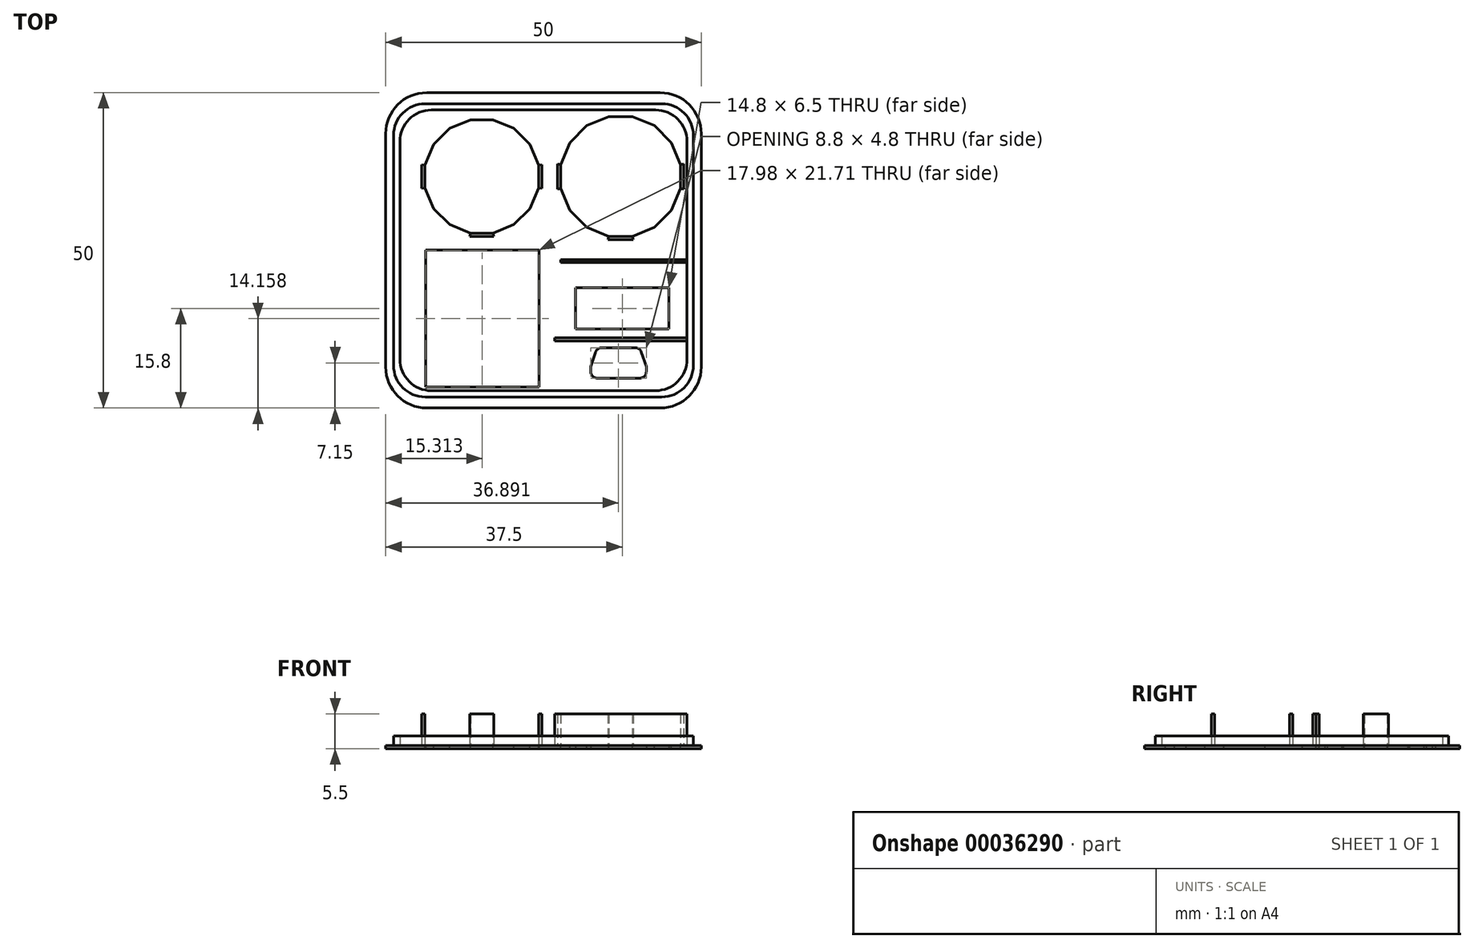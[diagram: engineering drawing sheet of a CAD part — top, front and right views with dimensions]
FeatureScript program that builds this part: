
annotation { "Feature Type Name" : "Feature", "Feature Type Description" : "" }
export const myFeature = defineFeature(function(context is Context, id is Id, definition is map)
    precondition{}
    {
        {
            var Q0;
            Q0=qCreatedBy(makeId("Top.planeOp"),FACE);
            var sketch = newSketch(context, id + "F0", { "sketchPlane" : qUnion([Q0])});
            skLineSegment(sketch, "E0.bottom", {"start": v(6.5, 0) * mm, "end": v(43.5, 0) * mm});
            skLineSegment(sketch, "E0.top", {"start": v(6.5, -50) * mm, "end": v(43.5, -50) * mm});
            skLineSegment(sketch, "E0.left", {"start": v(0, -6.5) * mm, "end": v(0, -43.5) * mm});
            skLineSegment(sketch, "E0.right", {"start": v(50, -6.5) * mm, "end": v(50, -43.5) * mm});
            skPoint(sketch, "E1.visualSharp", {"position": v(0, 0) * mm});
            skArc(sketch, "E1.filletArc", {"start": v(6.5, 0) * mm, "mid": v(1.9, -1.9) * mm, "end": v(0, -6.5) * mm});
            skPoint(sketch, "E2.visualSharp", {"position": v(50, 0) * mm});
            skArc(sketch, "E2.filletArc", {"start": v(50, -6.5) * mm, "mid": v(48.1, -1.9) * mm, "end": v(43.5, 0) * mm});
            skPoint(sketch, "E3.visualSharp", {"position": v(50, -50) * mm});
            skArc(sketch, "E3.filletArc", {"start": v(43.5, -50) * mm, "mid": v(48.1, -48.1) * mm, "end": v(50, -43.5) * mm});
            skPoint(sketch, "E4.visualSharp", {"position": v(0, -50) * mm});
            skArc(sketch, "E4.filletArc", {"start": v(0, -43.5) * mm, "mid": v(1.9, -48.1) * mm, "end": v(6.5, -50) * mm});
            skSolve(sketch);
        }
        {
            var Q0;
            Q0=qSketchRegion(id+"FKO5VP6ajgZ1Vob_0",true);
            var Q1;
            Q1=makeQuery(id+"F0.imprint","IMPRINT",FACE,{"disambiguationData":[TD([[makeQuery(id+"F0.imprint","IMPRINT",EDGE,{"derivedFrom":sQuery(id+"F0.wireOp",EDGE,"E0.bottom")}),-1.0]])]});
            extrude(context, id + "F1", {"entities" : qUnion([Q0, Q1]), "depth" : 0.5 * mm});
        }
        {
            var Q0;
            Q0=makeQuery(id+"F1.opExtrude","CAP_FACE",FACE,{"disambiguationData":[OSD([sQuery(id+"F0.wireOp",EDGE,"E0.bottom"),sQuery(id+"F0.wireOp",EDGE,"E0.top"),sQuery(id+"F0.wireOp",EDGE,"E0.left"),sQuery(id+"F0.wireOp",EDGE,"E0.right")])],"isStart":false});
            var sketch = newSketch(context, id + "F2", { "sketchPlane" : qUnion([Q0])});
            skLineSegment(sketch, "E5.bottom", {"start": v(6.25, -1.75) * mm, "end": v(43.75, -1.75) * mm});
            skLineSegment(sketch, "E5.top", {"start": v(6.25, -48.25) * mm, "end": v(43.75, -48.25) * mm});
            skLineSegment(sketch, "E5.left", {"start": v(1.25, -6.75) * mm, "end": v(1.25, -43.25) * mm});
            skLineSegment(sketch, "E5.right", {"start": v(48.75, -6.75) * mm, "end": v(48.75, -43.25) * mm});
            skLineSegment(sketch, "E6", {"start": v(25, 0) * mm, "end": v(25, -1.75) * mm, "construction": true});
            skLineSegment(sketch, "E7", {"start": v(25, -48.25) * mm, "end": v(25, -50) * mm, "construction": true});
            skLineSegment(sketch, "E8.0", {"start": v(7.25, -2.75) * mm, "end": v(42.75, -2.75) * mm});
            skLineSegment(sketch, "E8.1", {"start": v(2.25, -7.75) * mm, "end": v(2.25, -42.25) * mm});
            skLineSegment(sketch, "E8.2", {"start": v(7.25, -47.25) * mm, "end": v(42.75, -47.25) * mm});
            skLineSegment(sketch, "E8.3", {"start": v(47.75, -7.75) * mm, "end": v(47.75, -42.25) * mm});
            skPoint(sketch, "E9.visualSharp", {"position": v(2.25, -2.75) * mm});
            skArc(sketch, "E9.filletArc", {"start": v(7.25, -2.75) * mm, "mid": v(3.71, -4.21) * mm, "end": v(2.25, -7.75) * mm});
            skPoint(sketch, "E10.visualSharp", {"position": v(1.25, -1.75) * mm});
            skArc(sketch, "E10.filletArc", {"start": v(6.25, -1.75) * mm, "mid": v(2.71, -3.21) * mm, "end": v(1.25, -6.75) * mm});
            skPoint(sketch, "E11.visualSharp", {"position": v(48.75, -1.75) * mm});
            skArc(sketch, "E11.filletArc", {"start": v(48.75, -6.75) * mm, "mid": v(47.29, -3.21) * mm, "end": v(43.75, -1.75) * mm});
            skPoint(sketch, "E12.visualSharp", {"position": v(47.75, -2.75) * mm});
            skArc(sketch, "E12.filletArc", {"start": v(47.75, -7.75) * mm, "mid": v(46.29, -4.21) * mm, "end": v(42.75, -2.75) * mm});
            skPoint(sketch, "E13.visualSharp", {"position": v(47.75, -47.25) * mm});
            skArc(sketch, "E13.filletArc", {"start": v(42.75, -47.25) * mm, "mid": v(46.29, -45.79) * mm, "end": v(47.75, -42.25) * mm});
            skPoint(sketch, "E14.visualSharp", {"position": v(48.75, -48.25) * mm});
            skArc(sketch, "E14.filletArc", {"start": v(43.75, -48.25) * mm, "mid": v(47.29, -46.79) * mm, "end": v(48.75, -43.25) * mm});
            skPoint(sketch, "E15.visualSharp", {"position": v(2.25, -47.25) * mm});
            skArc(sketch, "E15.filletArc", {"start": v(2.25, -42.25) * mm, "mid": v(3.71, -45.79) * mm, "end": v(7.25, -47.25) * mm});
            skPoint(sketch, "E16.visualSharp", {"position": v(1.25, -48.25) * mm});
            skArc(sketch, "E16.filletArc", {"start": v(1.25, -43.25) * mm, "mid": v(2.71, -46.79) * mm, "end": v(6.25, -48.25) * mm});
            skSolve(sketch);
        }
        {
            var Q0;
            Q0=makeQuery(id+"F2.imprint","IMPRINT",FACE,{"disambiguationData":[TD([[makeQuery(id+"F2.imprint","IMPRINT",EDGE,{"derivedFrom":sQuery(id+"F2.wireOp",EDGE,"E5.bottom")}),1.0]])]});
            var sketch = newSketch(context, id + "F3", { "sketchPlane" : qUnion([Q0])});
            skSolve(sketch);
        }
        {
            var Q0;
            Q0=qSketchRegion(id+"F3",true);
            var Q1;
            Q1=makeQuery(id+"F2.imprint","IMPRINT",FACE,{"disambiguationData":[TD([[makeQuery(id+"F2.imprint","IMPRINT",EDGE,{"derivedFrom":sQuery(id+"F2.wireOp",EDGE,"E5.bottom")}),-1.0]])]});
            extrude(context, id + "F4", {"entities" : qUnion([Q0, Q1]), "operationType" : NewBodyOperationType.ADD, "depth" : 1.5 * mm});
        }
        {
            var Q0;
            Q0=makeQuery(id+"F1.opExtrude","CAP_FACE",FACE,{"disambiguationData":[OSD([sQuery(id+"F0.wireOp",EDGE,"E0.bottom"),sQuery(id+"F0.wireOp",EDGE,"E0.top"),sQuery(id+"F0.wireOp",EDGE,"E0.left"),sQuery(id+"F0.wireOp",EDGE,"E0.right"),sQuery(id+"F0.wireOp",EDGE,"E1.filletArc"),sQuery(id+"F0.wireOp",EDGE,"E2.filletArc"),sQuery(id+"F0.wireOp",EDGE,"E3.filletArc"),sQuery(id+"F0.wireOp",EDGE,"E4.filletArc")])],"isStart":true});
            var sketch = newSketch(context, id + "F5", { "sketchPlane" : qUnion([Q0])});
            skLineSegment(sketch, "E17.top", {"start": v(33.5, 45.25) * mm, "end": v(40.3, 45.25) * mm});
            skLineSegment(sketch, "E17.left", {"start": v(32.5, 43.45) * mm, "end": v(32.5, 44.25) * mm});
            skLineSegment(sketch, "E17.right", {"start": v(41.3, 43.45) * mm, "end": v(41.3, 44.25) * mm});
            skLineSegment(sketch, "E18.bottom", {"start": v(6.32, 24.99) * mm, "end": v(24.3, 24.99) * mm});
            skLineSegment(sketch, "E18.top", {"start": v(6.32, 46.7) * mm, "end": v(24.3, 46.7) * mm});
            skLineSegment(sketch, "E18.left", {"start": v(6.32, 24.99) * mm, "end": v(6.32, 46.7) * mm});
            skLineSegment(sketch, "E18.right", {"start": v(24.3, 24.99) * mm, "end": v(24.3, 46.7) * mm});
            skPoint(sketch, "E19.visualSharp", {"position": v(32.5, 45.25) * mm});
            skArc(sketch, "E19.filletArc", {"start": v(33.5, 45.25) * mm, "mid": v(32.78, 44.96) * mm, "end": v(32.5, 44.25) * mm});
            skPoint(sketch, "E20.visualSharp", {"position": v(41.3, 45.25) * mm});
            skArc(sketch, "E20.filletArc", {"start": v(41.3, 44.25) * mm, "mid": v(41, 44.96) * mm, "end": v(40.3, 45.25) * mm});
            skLineSegment(sketch, "E21", {"start": v(34.21, 40.45) * mm, "end": v(39.57, 40.45) * mm});
            skLineSegment(sketch, "E22", {"start": v(32.5, 43.45) * mm, "end": v(33.26, 41.13) * mm});
            skLineSegment(sketch, "E23", {"start": v(40.52, 41.13) * mm, "end": v(41.3, 43.45) * mm});
            skPoint(sketch, "E24.visualSharp", {"position": v(33.5, 40.45) * mm});
            skArc(sketch, "E24.filletArc", {"start": v(33.26, 41.13) * mm, "mid": v(33.63, 40.64) * mm, "end": v(34.21, 40.45) * mm});
            skPoint(sketch, "E25.visualSharp", {"position": v(40.3, 40.45) * mm});
            skArc(sketch, "E25.filletArc", {"start": v(39.57, 40.45) * mm, "mid": v(40.16, 40.64) * mm, "end": v(40.52, 41.13) * mm});
            skLineSegment(sketch, "E26.bottom", {"start": v(30.1, 37.45) * mm, "end": v(44.9, 37.45) * mm});
            skLineSegment(sketch, "E26.top", {"start": v(30.1, 30.95) * mm, "end": v(44.9, 30.95) * mm});
            skLineSegment(sketch, "E26.left", {"start": v(30.1, 37.45) * mm, "end": v(30.1, 30.95) * mm});
            skLineSegment(sketch, "E26.right", {"start": v(44.9, 37.45) * mm, "end": v(44.9, 30.95) * mm});
            skLineSegment(sketch, "E27", {"start": v(37, 40.45) * mm, "end": v(37, 39.95) * mm, "construction": true});
            skLineSegment(sketch, "E28", {"start": v(37.5, 30.95) * mm, "end": v(37.5, 26.61) * mm, "construction": true});
            skSolve(sketch);
        }
        {
            var Q0;
            Q0=makeQuery(id+"F5.imprint","IMPRINT",FACE,{"disambiguationData":[TD([[makeQuery(id+"F5.imprint","IMPRINT",EDGE,{"derivedFrom":sQuery(id+"F5.wireOp",EDGE,"E18.bottom")}),1.0]])]});
            var Q1;
            Q1=makeQuery(id+"F5.imprint","IMPRINT",FACE,{"disambiguationData":[TD([[makeQuery(id+"F5.imprint","IMPRINT",EDGE,{"derivedFrom":sQuery(id+"F5.wireOp",EDGE,"E17.top")}),-1.0]])]});
            var Q2;
            Q2=makeQuery(id+"F5.imprint","IMPRINT",FACE,{"disambiguationData":[TD([[makeQuery(id+"F5.imprint","IMPRINT",EDGE,{"derivedFrom":sQuery(id+"F5.wireOp",EDGE,"E26.bottom")}),-1.0]])]});
            extrude(context, id + "F6", {"entities" : qUnion([Q0, Q1, Q2]), "operationType" : NewBodyOperationType.REMOVE, "endBound" : BoundingType.UP_TO_NEXT, "oppositeDirection" : true, "depth" : 25 * mm});
        }
        {
            var Q0;
            Q0=makeQuery(id+"F3.imprint","IMPRINT",FACE,{"disambiguationData":[TD([[makeQuery(id+"F3.imprint","IMPRINT",EDGE,{"derivedFrom":makeQuery(id+"F2.imprint","IMPRINT",EDGE,{"derivedFrom":sQuery(id+"F2.wireOp",EDGE,"E5.bottom")})}),-1.0]])]});
            var sketch = newSketch(context, id + "F7", { "sketchPlane" : qUnion([Q0])});
            skLineSegment(sketch, "E29.bottom", {"start": v(47.75, -39.35) * mm, "end": v(26.75, -39.35) * mm});
            skLineSegment(sketch, "E29.top", {"start": v(47.75, -38.85) * mm, "end": v(26.75, -38.85) * mm});
            skLineSegment(sketch, "E29.left", {"start": v(47.75, -39.35) * mm, "end": v(47.75, -38.85) * mm});
            skLineSegment(sketch, "E29.right", {"start": v(26.75, -39.35) * mm, "end": v(26.75, -38.85) * mm});
            skLineSegment(sketch, "E30.bottom", {"start": v(47.75, -26.95) * mm, "end": v(27.75, -26.95) * mm});
            skLineSegment(sketch, "E30.top", {"start": v(47.75, -26.45) * mm, "end": v(27.75, -26.45) * mm});
            skLineSegment(sketch, "E30.left", {"start": v(47.75, -26.95) * mm, "end": v(47.75, -26.45) * mm});
            skLineSegment(sketch, "E30.right", {"start": v(27.75, -26.95) * mm, "end": v(27.75, -26.45) * mm});
            skLineSegment(sketch, "E31", {"start": v(37.25, -39.35) * mm, "end": v(37.25, -39.85) * mm, "construction": true});
            skLineSegment(sketch, "E32", {"start": v(37.75, -26.95) * mm, "end": v(37.75, -27.9) * mm});
            skSolve(sketch);
        }
        {
            var Q0;
            Q0=qSketchRegion(id+"F7",true);
            extrude(context, id + "F8", {"entities" : qUnion([Q0]), "operationType" : NewBodyOperationType.ADD, "depth" : 5 * mm});
        }
        {
            var Q0;
            Q0=makeQuery(id+"F3.imprint","IMPRINT",FACE,{"disambiguationData":[TD([[makeQuery(id+"F3.imprint","IMPRINT",EDGE,{"derivedFrom":makeQuery(id+"F2.imprint","IMPRINT",EDGE,{"derivedFrom":sQuery(id+"F2.wireOp",EDGE,"E5.bottom")})}),-1.0]])]});
            var sketch = newSketch(context, id + "F9", { "sketchPlane" : qUnion([Q0])});
            skLineSegment(sketch, "E33.4", {"start": v(29.18, -18.67) * mm, "end": v(27.73, -15.18) * mm});
            skLineSegment(sketch, "E34", {"start": v(42.62, -21.34) * mm, "end": v(42.9, -21.77) * mm});
            skLineSegment(sketch, "E35.11", {"start": v(24.22, -15.08) * mm, "end": v(22.84, -18.39) * mm});
            skLineSegment(sketch, "E36.7", {"start": v(27.23, -15.28) * mm, "end": v(27.23, -11.3) * mm});
            skLineSegment(sketch, "E37.12", {"start": v(17.1, -3.8) * mm, "end": v(20.6, -5.24) * mm});
            skLineSegment(sketch, "E33.15", {"start": v(39.12, -3.8) * mm, "end": v(42.62, -5.24) * mm});
            skLineSegment(sketch, "E33.14", {"start": v(42.62, -5.24) * mm, "end": v(45.29, -7.9) * mm});
            skLineSegment(sketch, "E37.2", {"start": v(20.6, -21.34) * mm, "end": v(17.1, -22.8) * mm});
            skLineSegment(sketch, "E35.8", {"start": v(17, -22.3) * mm, "end": v(13.42, -22.3) * mm});
            skLineSegment(sketch, "E36.6", {"start": v(28.76, -18.95) * mm, "end": v(27.23, -15.28) * mm});
            skLineSegment(sketch, "E38", {"start": v(17, -22.3) * mm, "end": v(17.1, -22.8) * mm});
            skLineSegment(sketch, "E36.1", {"start": v(45.71, -18.95) * mm, "end": v(42.9, -21.77) * mm});
            skLineSegment(sketch, "E39", {"start": v(35.34, -22.8) * mm, "end": v(35.24, -23.3) * mm});
            skLineSegment(sketch, "E36.0", {"start": v(47.23, -15.28) * mm, "end": v(45.71, -18.95) * mm});
            skLineSegment(sketch, "E35.1", {"start": v(7.59, -8.2) * mm, "end": v(10.12, -5.66) * mm});
            skLineSegment(sketch, "E35.15", {"start": v(17, -4.3) * mm, "end": v(20.31, -5.66) * mm});
            skLineSegment(sketch, "E35.12", {"start": v(24.22, -11.5) * mm, "end": v(24.22, -15.08) * mm});
            skLineSegment(sketch, "E33.3", {"start": v(27.73, -15.18) * mm, "end": v(27.73, -11.4) * mm});
            skLineSegment(sketch, "E33.1", {"start": v(29.18, -7.9) * mm, "end": v(31.85, -5.24) * mm});
            skLineSegment(sketch, "E40", {"start": v(23.27, -18.67) * mm, "end": v(22.84, -18.39) * mm});
            skLineSegment(sketch, "E36.14", {"start": v(45.71, -7.63) * mm, "end": v(47.23, -11.3) * mm});
            skLineSegment(sketch, "E37.13", {"start": v(20.6, -5.24) * mm, "end": v(23.27, -7.9) * mm});
            skCircle(sketch, "E36.cCircle", {"center": v(37.23, -13.3) * mm, "radius": 10 * mm, "construction": true});
            skLineSegment(sketch, "E33.7", {"start": v(35.34, -22.8) * mm, "end": v(31.85, -21.34) * mm});
            skLineSegment(sketch, "E36.3", {"start": v(39.22, -23.3) * mm, "end": v(35.24, -23.3) * mm});
            skLineSegment(sketch, "E36.9", {"start": v(28.76, -7.63) * mm, "end": v(31.57, -4.81) * mm});
            skLineSegment(sketch, "E35.3", {"start": v(6.22, -15.08) * mm, "end": v(6.22, -11.5) * mm});
            skLineSegment(sketch, "E35.0", {"start": v(10.12, -5.66) * mm, "end": v(13.42, -4.3) * mm});
            skLineSegment(sketch, "E36.5", {"start": v(31.57, -21.77) * mm, "end": v(28.76, -18.95) * mm});
            skLineSegment(sketch, "E35.14", {"start": v(20.31, -5.66) * mm, "end": v(22.84, -8.2) * mm});
            skLineSegment(sketch, "E36.12", {"start": v(39.22, -3.3) * mm, "end": v(42.9, -4.81) * mm});
            skLineSegment(sketch, "E33.8", {"start": v(39.12, -22.8) * mm, "end": v(35.34, -22.8) * mm});
            skLineSegment(sketch, "E37.10", {"start": v(9.83, -5.24) * mm, "end": v(13.33, -3.8) * mm});
            skLineSegment(sketch, "E35.13", {"start": v(22.84, -8.2) * mm, "end": v(24.22, -11.5) * mm});
            skLineSegment(sketch, "E37.15", {"start": v(24.72, -11.4) * mm, "end": v(24.72, -15.18) * mm});
            skLineSegment(sketch, "E37.1", {"start": v(23.27, -18.67) * mm, "end": v(20.6, -21.34) * mm});
            skLineSegment(sketch, "E35.4", {"start": v(7.59, -18.39) * mm, "end": v(6.22, -15.08) * mm});
            skLineSegment(sketch, "E37.9", {"start": v(7.16, -7.9) * mm, "end": v(9.83, -5.24) * mm});
            skLineSegment(sketch, "E37.8", {"start": v(5.72, -11.4) * mm, "end": v(7.16, -7.9) * mm});
            skLineSegment(sketch, "E36.2", {"start": v(42.9, -21.77) * mm, "end": v(39.22, -23.3) * mm});
            skLineSegment(sketch, "E37.3", {"start": v(17.1, -22.8) * mm, "end": v(13.33, -22.8) * mm});
            skLineSegment(sketch, "E37.7", {"start": v(5.72, -15.18) * mm, "end": v(5.72, -11.4) * mm});
            skLineSegment(sketch, "E35.10", {"start": v(22.84, -18.39) * mm, "end": v(20.31, -20.92) * mm});
            skLineSegment(sketch, "E36.10", {"start": v(31.57, -4.81) * mm, "end": v(35.24, -3.3) * mm});
            skLineSegment(sketch, "E37.5", {"start": v(9.83, -21.34) * mm, "end": v(7.16, -18.67) * mm});
            skLineSegment(sketch, "E35.9", {"start": v(20.31, -20.92) * mm, "end": v(17, -22.3) * mm});
            skLineSegment(sketch, "E33.10", {"start": v(45.29, -18.67) * mm, "end": v(42.62, -21.34) * mm});
            skLineSegment(sketch, "E37.6", {"start": v(7.16, -18.67) * mm, "end": v(5.72, -15.18) * mm});
            skLineSegment(sketch, "E33.13", {"start": v(45.29, -7.9) * mm, "end": v(46.73, -11.4) * mm});
            skLineSegment(sketch, "E36.4", {"start": v(35.24, -23.3) * mm, "end": v(31.57, -21.77) * mm});
            skLineSegment(sketch, "E33.0", {"start": v(31.85, -5.24) * mm, "end": v(35.34, -3.8) * mm});
            skLineSegment(sketch, "E33.12", {"start": v(46.73, -11.4) * mm, "end": v(46.73, -15.18) * mm});
            skLineSegment(sketch, "E36.8", {"start": v(27.23, -11.3) * mm, "end": v(28.76, -7.63) * mm});
            skLineSegment(sketch, "E41", {"start": v(13.33, -22.8) * mm, "end": v(13.42, -22.3) * mm});
            skLineSegment(sketch, "E33.6", {"start": v(31.85, -21.34) * mm, "end": v(29.18, -18.67) * mm});
            skLineSegment(sketch, "E33.11", {"start": v(46.73, -15.18) * mm, "end": v(45.29, -18.67) * mm});
            skLineSegment(sketch, "E37.4", {"start": v(13.33, -22.8) * mm, "end": v(9.83, -21.34) * mm});
            skLineSegment(sketch, "E36.13", {"start": v(42.9, -4.81) * mm, "end": v(45.71, -7.63) * mm});
            skPoint(sketch, "E37.0.midPoint", {"position": v(24, -16.93) * mm});
            skLineSegment(sketch, "E33.9", {"start": v(42.62, -21.34) * mm, "end": v(39.12, -22.8) * mm});
            skLineSegment(sketch, "E42", {"start": v(20.6, -21.34) * mm, "end": v(20.31, -20.92) * mm});
            skLineSegment(sketch, "E36.15", {"start": v(47.23, -11.3) * mm, "end": v(47.23, -15.28) * mm});
            skLineSegment(sketch, "E35.6", {"start": v(10.12, -20.92) * mm, "end": v(7.59, -18.39) * mm});
            skLineSegment(sketch, "E33.2", {"start": v(27.73, -11.4) * mm, "end": v(29.18, -7.9) * mm});
            skLineSegment(sketch, "E43", {"start": v(39.12, -22.8) * mm, "end": v(39.22, -23.3) * mm});
            skCircle(sketch, "E37.cCircle", {"center": v(15.22, -13.3) * mm, "radius": 9.5 * mm, "construction": true});
            skLineSegment(sketch, "E35.2", {"start": v(6.22, -11.5) * mm, "end": v(7.59, -8.2) * mm});
            skPoint(sketch, "E36.0.midPoint", {"position": v(46.47, -17.12) * mm});
            skLineSegment(sketch, "E37.14", {"start": v(23.27, -7.9) * mm, "end": v(24.72, -11.4) * mm});
            skLineSegment(sketch, "E37.11", {"start": v(13.33, -3.8) * mm, "end": v(17.1, -3.8) * mm});
            skLineSegment(sketch, "E37.0", {"start": v(24.72, -15.18) * mm, "end": v(23.27, -18.67) * mm});
            skLineSegment(sketch, "E33.5", {"start": v(35.34, -3.8) * mm, "end": v(39.12, -3.8) * mm});
            skLineSegment(sketch, "E35.7", {"start": v(13.42, -22.3) * mm, "end": v(10.12, -20.92) * mm});
            skLineSegment(sketch, "E44", {"start": v(35.34, -3.8) * mm, "end": v(35.24, -3.3) * mm});
            skLineSegment(sketch, "E45", {"start": v(13.33, -3.8) * mm, "end": v(13.42, -4.3) * mm});
            skLineSegment(sketch, "E46", {"start": v(39.22, -3.3) * mm, "end": v(39.12, -3.8) * mm});
            skLineSegment(sketch, "E47", {"start": v(17, -4.3) * mm, "end": v(17.1, -3.8) * mm});
            skLineSegment(sketch, "E36.11", {"start": v(35.24, -3.3) * mm, "end": v(39.22, -3.3) * mm});
            skLineSegment(sketch, "E48", {"start": v(10.12, -5.66) * mm, "end": v(9.83, -5.24) * mm});
            skLineSegment(sketch, "E49", {"start": v(31.57, -4.81) * mm, "end": v(31.85, -5.24) * mm});
            skLineSegment(sketch, "E35.5", {"start": v(13.42, -4.3) * mm, "end": v(17, -4.3) * mm});
            skLineSegment(sketch, "E50", {"start": v(7.16, -7.9) * mm, "end": v(7.59, -8.2) * mm});
            skLineSegment(sketch, "E51", {"start": v(31.57, -21.77) * mm, "end": v(31.85, -21.34) * mm});
            skLineSegment(sketch, "E52", {"start": v(45.71, -7.63) * mm, "end": v(45.29, -7.9) * mm});
            skLineSegment(sketch, "E53", {"start": v(46.73, -15.18) * mm, "end": v(47.23, -15.28) * mm});
            skLineSegment(sketch, "E54", {"start": v(46.73, -11.4) * mm, "end": v(47.23, -11.3) * mm});
            skLineSegment(sketch, "E55", {"start": v(22.84, -8.2) * mm, "end": v(23.27, -7.9) * mm});
            skLineSegment(sketch, "E56", {"start": v(42.62, -5.24) * mm, "end": v(42.9, -4.81) * mm});
            skLineSegment(sketch, "E57", {"start": v(7.59, -18.39) * mm, "end": v(7.16, -18.67) * mm});
            skLineSegment(sketch, "E58", {"start": v(28.76, -18.95) * mm, "end": v(29.18, -18.67) * mm});
            skLineSegment(sketch, "E59", {"start": v(20.6, -5.24) * mm, "end": v(20.31, -5.66) * mm});
            skLineSegment(sketch, "E60", {"start": v(29.18, -7.9) * mm, "end": v(28.76, -7.63) * mm});
            skLineSegment(sketch, "E61", {"start": v(24.22, -15.08) * mm, "end": v(24.72, -15.18) * mm});
            skLineSegment(sketch, "E62", {"start": v(27.23, -11.3) * mm, "end": v(27.73, -11.4) * mm});
            skLineSegment(sketch, "E63", {"start": v(27.73, -15.18) * mm, "end": v(27.23, -15.28) * mm});
            skLineSegment(sketch, "E64", {"start": v(24.72, -11.4) * mm, "end": v(24.22, -11.5) * mm});
            skLineSegment(sketch, "E65", {"start": v(5.72, -11.4) * mm, "end": v(6.22, -11.5) * mm});
            skLineSegment(sketch, "E66", {"start": v(5.72, -15.18) * mm, "end": v(6.22, -15.08) * mm});
            skLineSegment(sketch, "E67", {"start": v(9.83, -21.34) * mm, "end": v(10.12, -20.92) * mm});
            skLineSegment(sketch, "E68", {"start": v(45.71, -18.95) * mm, "end": v(45.29, -18.67) * mm});
            skCircle(sketch, "E69", {"center": v(37.23, -13.3) * mm, "radius": 9.5 * mm, "construction": true});
            skCircle(sketch, "E70", {"center": v(15.22, -13.3) * mm, "radius": 9 * mm, "construction": true});
            skSolve(sketch);
        }
        {
            var Q0;
            Q0=makeQuery(id+"F9.imprint","IMPRINT",FACE,{"disambiguationData":[TD([[makeQuery(id+"F9.imprint","IMPRINT",EDGE,{"derivedFrom":sQuery(id+"F9.wireOp",EDGE,"E33.12")}),1.0]])]});
            var Q1;
            Q1=makeQuery(id+"F9.imprint","IMPRINT",FACE,{"disambiguationData":[TD([[makeQuery(id+"F9.imprint","IMPRINT",EDGE,{"derivedFrom":sQuery(id+"F9.wireOp",EDGE,"E39")}),1.0]])]});
            var Q2;
            Q2=makeQuery(id+"F9.imprint","IMPRINT",FACE,{"disambiguationData":[TD([[makeQuery(id+"F9.imprint","IMPRINT",EDGE,{"derivedFrom":sQuery(id+"F9.wireOp",EDGE,"E36.7")}),-1.0]])]});
            var Q3;
            Q3=makeQuery(id+"F9.imprint","IMPRINT",FACE,{"disambiguationData":[TD([[makeQuery(id+"F9.imprint","IMPRINT",EDGE,{"derivedFrom":sQuery(id+"F9.wireOp",EDGE,"E35.8")}),1.0]])]});
            var Q4;
            Q4=makeQuery(id+"F9.imprint","IMPRINT",FACE,{"disambiguationData":[TD([[makeQuery(id+"F9.imprint","IMPRINT",EDGE,{"derivedFrom":sQuery(id+"F9.wireOp",EDGE,"E35.12")}),1.0]])]});
            var Q5;
            Q5=makeQuery(id+"F9.imprint","IMPRINT",FACE,{"disambiguationData":[TD([[makeQuery(id+"F9.imprint","IMPRINT",EDGE,{"derivedFrom":sQuery(id+"F9.wireOp",EDGE,"E35.3")}),1.0]])]});
            extrude(context, id + "F10", {"entities" : qUnion([Q0, Q1, Q2, Q3, Q4, Q5]), "operationType" : NewBodyOperationType.ADD, "depth" : 5 * mm});
        }
        {
            var Q0;
            Q0=makeQuery(id+"F9.imprint","IMPRINT",FACE,{"disambiguationData":[TD([[makeQuery(id+"F9.imprint","IMPRINT",EDGE,{"derivedFrom":sQuery(id+"F9.wireOp",EDGE,"E33.4")}),-1.0]])]});
            extrude(context, id + "F11", {"entities" : qUnion([Q0]), "operationType" : NewBodyOperationType.REMOVE, "endBound" : BoundingType.UP_TO_NEXT, "oppositeDirection" : true, "depth" : 25 * mm});
        }
        {
            var Q0;
            Q0=makeQuery(id+"F9.imprint","IMPRINT",FACE,{"disambiguationData":[TD([[makeQuery(id+"F9.imprint","IMPRINT",EDGE,{"derivedFrom":sQuery(id+"F9.wireOp",EDGE,"E35.11")}),-1.0]])]});
            extrude(context, id + "F12", {"entities" : qUnion([Q0]), "operationType" : NewBodyOperationType.REMOVE, "endBound" : BoundingType.UP_TO_NEXT, "oppositeDirection" : true, "depth" : 25 * mm});
        }
    });
